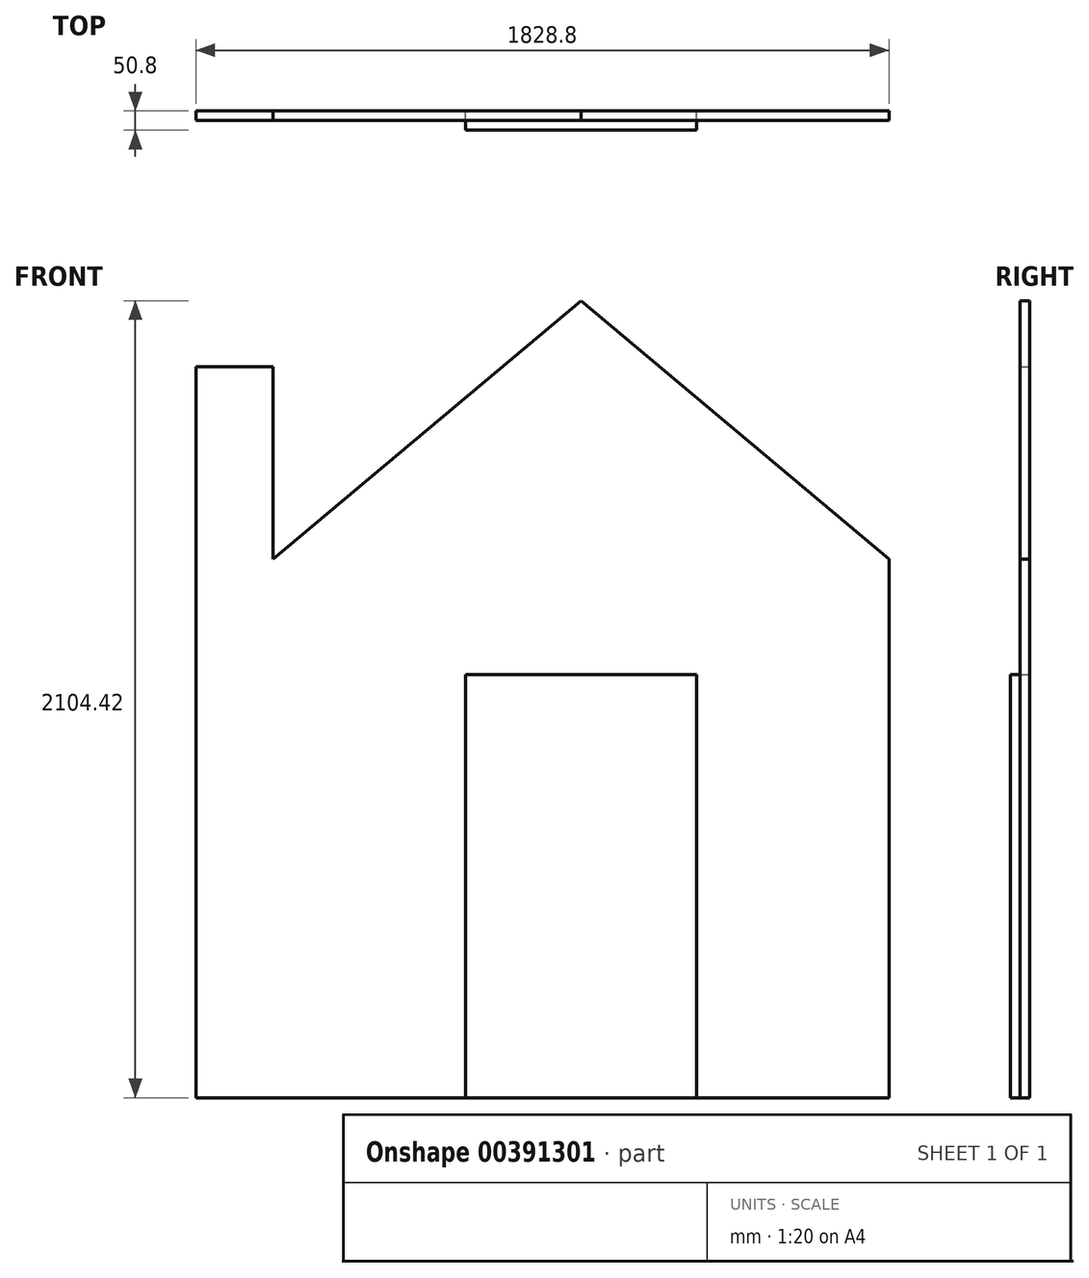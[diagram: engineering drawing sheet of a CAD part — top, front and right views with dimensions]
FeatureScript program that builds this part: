
annotation { "Feature Type Name" : "Feature", "Feature Type Description" : "" }
export const myFeature = defineFeature(function(context is Context, id is Id, definition is map)
    precondition{}
    {
        {
            var Q0;
            Q0=qCreatedBy(makeId("Front.planeOp"),FACE);
            var sketch = newSketch(context, id + "F0", { "sketchPlane" : qUnion([Q0])});
            skLineSegment(sketch, "E0.bottom", {"start": v(0, 0) * mm, "end": v(-1219.2, 0) * mm, "construction": true});
            skLineSegment(sketch, "E0.top", {"start": v(0, 2438.4) * mm, "end": v(-1219.2, 2438.4) * mm, "construction": true});
            skLineSegment(sketch, "E0.left", {"start": v(0, 0) * mm, "end": v(0, 2438.4) * mm, "construction": true});
            skLineSegment(sketch, "E0.right", {"start": v(-1219.2, 0) * mm, "end": v(-1219.2, 2438.4) * mm, "construction": true});
            skLineSegment(sketch, "E1.bottom", {"start": v(0, 0) * mm, "end": v(1219.2, 0) * mm, "construction": true});
            skLineSegment(sketch, "E1.top", {"start": v(0, 2438.4) * mm, "end": v(1219.2, 2438.4) * mm, "construction": true});
            skLineSegment(sketch, "E1.right", {"start": v(1219.2, 0) * mm, "end": v(1219.2, 2438.4) * mm, "construction": true});
            skLineSegment(sketch, "E2.bottom", {"start": v(914.4, 1574.8) * mm, "end": v(-914.4, 1574.8) * mm});
            skLineSegment(sketch, "E2.top", {"start": v(914.4, 152.4) * mm, "end": v(-914.4, 152.4) * mm});
            skLineSegment(sketch, "E2.left", {"start": v(914.4, 1574.8) * mm, "end": v(914.4, 152.4) * mm});
            skLineSegment(sketch, "E2.right", {"start": v(-914.4, 1574.8) * mm, "end": v(-914.4, 152.4) * mm});
            skPoint(sketch, "E2.middle", {"position": v(0, 863.6) * mm});
            skLineSegment(sketch, "E3.bottom", {"start": v(-914.4, 1574.8) * mm, "end": v(-711.2, 1574.8) * mm});
            skLineSegment(sketch, "E3.top", {"start": v(-914.4, 2082.8) * mm, "end": v(-711.2, 2082.8) * mm});
            skLineSegment(sketch, "E3.left", {"start": v(-914.4, 1574.8) * mm, "end": v(-914.4, 2082.8) * mm});
            skLineSegment(sketch, "E3.right", {"start": v(-711.2, 1574.8) * mm, "end": v(-711.2, 2082.8) * mm});
            skLineSegment(sketch, "E4", {"start": v(-711.2, 1574.8) * mm, "end": v(101.6, 2256.82) * mm});
            skLineSegment(sketch, "E5", {"start": v(101.6, 2256.82) * mm, "end": v(914.4, 1574.8) * mm});
            skLineSegment(sketch, "E6", {"start": v(101.6, 2256.82) * mm, "end": v(101.6, 1574.8) * mm, "construction": true});
            skLineSegment(sketch, "E7", {"start": v(101.6, 1574.8) * mm, "end": v(101.6, 152.4) * mm, "construction": true});
            skLineSegment(sketch, "E8.bottom", {"start": v(406.4, 1270) * mm, "end": v(-203.2, 1270) * mm});
            skLineSegment(sketch, "E8.top", {"start": v(406.4, 152.4) * mm, "end": v(-203.2, 152.4) * mm});
            skLineSegment(sketch, "E8.left", {"start": v(406.4, 1270) * mm, "end": v(406.4, 152.4) * mm});
            skLineSegment(sketch, "E8.right", {"start": v(-203.2, 1270) * mm, "end": v(-203.2, 152.4) * mm});
            skPoint(sketch, "E8.middle", {"position": v(101.6, 711.2) * mm});
            skSolve(sketch);
        }
        {
            var Q0;
            Q0=makeQuery(id+"F0.imprint","IMPRINT",FACE,{"disambiguationData":[TD([[makeQuery(id+"F0.imprint","IMPRINT",EDGE,{"derivedFrom":sQuery(id+"F0.wireOp",EDGE,"E8.bottom")}),1.0]])]});
            extrude(context, id + "F1", {"entities" : qUnion([Q0]), "depth" : 50.8 * mm});
        }
        {
            var Q0;
            Q0 = qSketchRegion(id + "F0", true);
            extrude(context, id + "F2", {"entities" : qUnion([Q0]), "depth" : 25.4 * mm});
        }
    });
